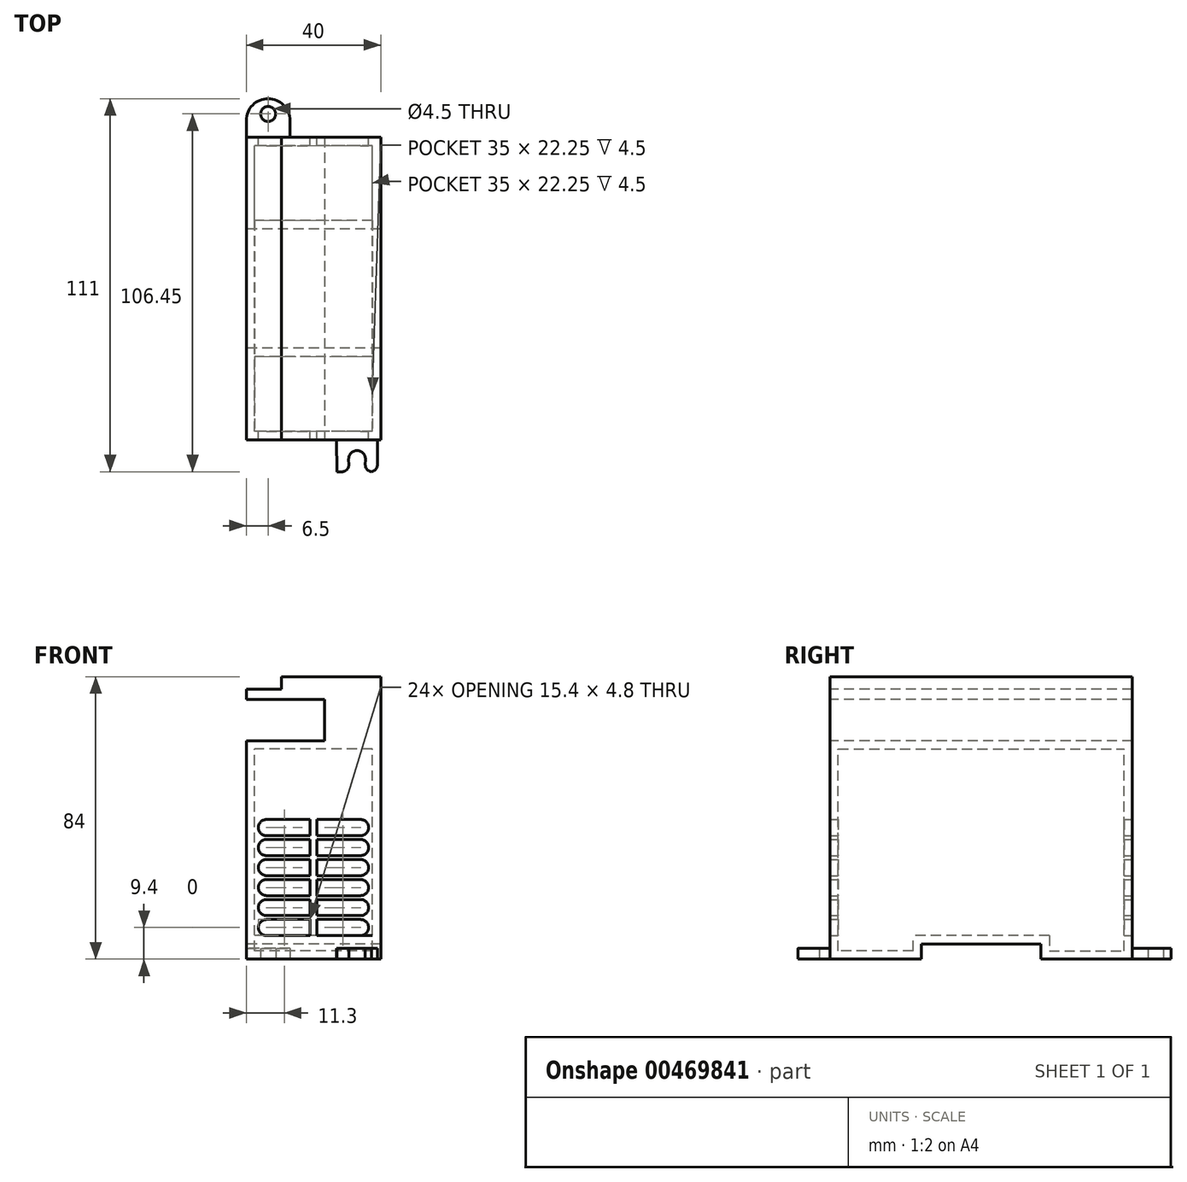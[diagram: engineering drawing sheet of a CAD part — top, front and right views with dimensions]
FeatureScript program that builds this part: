
annotation { "Feature Type Name" : "Feature", "Feature Type Description" : "" }
export const myFeature = defineFeature(function(context is Context, id is Id, definition is map)
    precondition{}
    {
        {
            var Q0;
            Q0=qCreatedBy(makeId("Right.planeOp"),FACE);
            var sketch = newSketch(context, id + "F0", { "sketchPlane" : qUnion([Q0])});
            skLineSegment(sketch, "E0", {"start": v(-17.75, 0) * mm, "end": v(-45, 0) * mm});
            skLineSegment(sketch, "E1", {"start": v(17.75, 0) * mm, "end": v(45, 0) * mm});
            skLineSegment(sketch, "E2", {"start": v(-45, 0) * mm, "end": v(-45, 65) * mm});
            skLineSegment(sketch, "E3", {"start": v(45, 0) * mm, "end": v(45, 65) * mm});
            skLineSegment(sketch, "E4", {"start": v(-45, 65) * mm, "end": v(45, 65) * mm});
            skLineSegment(sketch, "E5", {"start": v(-17.75, 0) * mm, "end": v(-17.75, 4.5) * mm});
            skLineSegment(sketch, "E6", {"start": v(17.75, 4.5) * mm, "end": v(17.75, 0) * mm});
            skLineSegment(sketch, "E7", {"start": v(17.75, 4.5) * mm, "end": v(-17.75, 4.5) * mm});
            skSolve(sketch);
        }
        {
            var Q0;
            Q0=makeQuery(id+"F0.imprint","IMPRINT",FACE,{"disambiguationData":[TD([[makeQuery(id+"F0.imprint","IMPRINT",EDGE,{"derivedFrom":sQuery(id+"F0.wireOp",EDGE,"E0")}),-1.0]])]});
            extrude(context, id + "F1", {"entities" : qUnion([Q0]), "depth" : 40 * mm});
        }
        {
            var Q0;
            Q0=makeQuery(id+"F1.opExtrude","SWEPT_FACE",FACE,{"disambiguationData":[OSD([sQuery(id+"F0.wireOp",EDGE,"E3")])]});
            var sketch = newSketch(context, id + "F2", { "sketchPlane" : qUnion([Q0])});
            skLineSegment(sketch, "E8", {"start": v(-20, 0) * mm, "end": v(-20, 7) * mm});
            skLineSegment(sketch, "E9", {"start": v(-19, 7) * mm, "end": v(-21, 7) * mm});
            skLineSegment(sketch, "E10", {"start": v(-21, 7) * mm, "end": v(-21, 11.8) * mm});
            skLineSegment(sketch, "E11", {"start": v(-21, 11.8) * mm, "end": v(-34, 11.8) * mm});
            skLineSegment(sketch, "E12", {"start": v(-21, 7) * mm, "end": v(-34, 7) * mm});
            skArc(sketch, "E13", {"start": v(-34, 7) * mm, "mid": v(-36.4, 9.4) * mm, "end": v(-34, 11.8) * mm});
            skPoint(sketch, "E13.centerSnap0", {"position": v(-21, 9.4) * mm});
            skLineSegment(sketch, "E14.MirrorCS", {"start": v(-19, 11.8) * mm, "end": v(-6, 11.8) * mm});
            skLineSegment(sketch, "E15.MirrorCS", {"start": v(-19, 7) * mm, "end": v(-19, 11.8) * mm});
            skLineSegment(sketch, "E16.MirrorCS", {"start": v(-19, 7) * mm, "end": v(-6, 7) * mm});
            skArc(sketch, "E17.MirrorCS", {"start": v(-6, 7) * mm, "mid": v(-3.6, 9.4) * mm, "end": v(-6, 11.8) * mm});
            skLineSegment(sketch, "E18.0.1.0", {"start": v(-21, 17.75) * mm, "end": v(-34, 17.75) * mm});
            skArc(sketch, "E18.0.1.1", {"start": v(-34, 12.95) * mm, "mid": v(-36.4, 15.35) * mm, "end": v(-34, 17.75) * mm});
            skLineSegment(sketch, "E18.0.1.2", {"start": v(-21, 12.95) * mm, "end": v(-34, 12.95) * mm});
            skLineSegment(sketch, "E18.0.1.3", {"start": v(-21, 12.95) * mm, "end": v(-21, 17.75) * mm});
            skLineSegment(sketch, "E18.0.1.4", {"start": v(-19, 12.95) * mm, "end": v(-19, 17.75) * mm});
            skLineSegment(sketch, "E18.0.1.5", {"start": v(-19, 12.95) * mm, "end": v(-6, 12.95) * mm});
            skArc(sketch, "E18.0.1.6", {"start": v(-6, 12.95) * mm, "mid": v(-3.6, 15.35) * mm, "end": v(-6, 17.75) * mm});
            skLineSegment(sketch, "E18.0.1.7", {"start": v(-19, 17.75) * mm, "end": v(-6, 17.75) * mm});
            skLineSegment(sketch, "E18.0.2.0", {"start": v(-21, 23.7) * mm, "end": v(-34, 23.7) * mm});
            skArc(sketch, "E18.0.2.1", {"start": v(-34, 18.9) * mm, "mid": v(-36.4, 21.3) * mm, "end": v(-34, 23.7) * mm});
            skLineSegment(sketch, "E18.0.2.2", {"start": v(-21, 18.9) * mm, "end": v(-34, 18.9) * mm});
            skLineSegment(sketch, "E18.0.2.3", {"start": v(-21, 18.9) * mm, "end": v(-21, 23.7) * mm});
            skLineSegment(sketch, "E18.0.2.4", {"start": v(-19, 18.9) * mm, "end": v(-19, 23.7) * mm});
            skLineSegment(sketch, "E18.0.2.5", {"start": v(-19, 18.9) * mm, "end": v(-6, 18.9) * mm});
            skArc(sketch, "E18.0.2.6", {"start": v(-6, 18.9) * mm, "mid": v(-3.6, 21.3) * mm, "end": v(-6, 23.7) * mm});
            skLineSegment(sketch, "E18.0.2.7", {"start": v(-19, 23.7) * mm, "end": v(-6, 23.7) * mm});
            skLineSegment(sketch, "E18.0.3.0", {"start": v(-21, 29.65) * mm, "end": v(-34, 29.65) * mm});
            skArc(sketch, "E18.0.3.1", {"start": v(-34, 24.85) * mm, "mid": v(-36.4, 27.25) * mm, "end": v(-34, 29.65) * mm});
            skLineSegment(sketch, "E18.0.3.2", {"start": v(-21, 24.85) * mm, "end": v(-34, 24.85) * mm});
            skLineSegment(sketch, "E18.0.3.3", {"start": v(-21, 24.85) * mm, "end": v(-21, 29.65) * mm});
            skLineSegment(sketch, "E18.0.3.4", {"start": v(-19, 24.85) * mm, "end": v(-19, 29.65) * mm});
            skLineSegment(sketch, "E18.0.3.5", {"start": v(-19, 24.85) * mm, "end": v(-6, 24.85) * mm});
            skArc(sketch, "E18.0.3.6", {"start": v(-6, 24.85) * mm, "mid": v(-3.6, 27.25) * mm, "end": v(-6, 29.65) * mm});
            skLineSegment(sketch, "E18.0.3.7", {"start": v(-19, 29.65) * mm, "end": v(-6, 29.65) * mm});
            skLineSegment(sketch, "E18.0.4.0", {"start": v(-21, 35.6) * mm, "end": v(-34, 35.6) * mm});
            skArc(sketch, "E18.0.4.1", {"start": v(-34, 30.8) * mm, "mid": v(-36.4, 33.2) * mm, "end": v(-34, 35.6) * mm});
            skLineSegment(sketch, "E18.0.4.2", {"start": v(-21, 30.8) * mm, "end": v(-34, 30.8) * mm});
            skLineSegment(sketch, "E18.0.4.3", {"start": v(-21, 30.8) * mm, "end": v(-21, 35.6) * mm});
            skLineSegment(sketch, "E18.0.4.4", {"start": v(-19, 30.8) * mm, "end": v(-19, 35.6) * mm});
            skLineSegment(sketch, "E18.0.4.5", {"start": v(-19, 30.8) * mm, "end": v(-6, 30.8) * mm});
            skArc(sketch, "E18.0.4.6", {"start": v(-6, 30.8) * mm, "mid": v(-3.6, 33.2) * mm, "end": v(-6, 35.6) * mm});
            skLineSegment(sketch, "E18.0.4.7", {"start": v(-19, 35.6) * mm, "end": v(-6, 35.6) * mm});
            skLineSegment(sketch, "E18.0.5.0", {"start": v(-21, 41.55) * mm, "end": v(-34, 41.55) * mm});
            skArc(sketch, "E18.0.5.1", {"start": v(-34, 36.75) * mm, "mid": v(-36.4, 39.15) * mm, "end": v(-34, 41.55) * mm});
            skLineSegment(sketch, "E18.0.5.2", {"start": v(-21, 36.75) * mm, "end": v(-34, 36.75) * mm});
            skLineSegment(sketch, "E18.0.5.3", {"start": v(-21, 36.75) * mm, "end": v(-21, 41.55) * mm});
            skLineSegment(sketch, "E18.0.5.4", {"start": v(-19, 36.75) * mm, "end": v(-19, 41.55) * mm});
            skLineSegment(sketch, "E18.0.5.5", {"start": v(-19, 36.75) * mm, "end": v(-6, 36.75) * mm});
            skArc(sketch, "E18.0.5.6", {"start": v(-6, 36.75) * mm, "mid": v(-3.6, 39.15) * mm, "end": v(-6, 41.55) * mm});
            skLineSegment(sketch, "E18.0.5.7", {"start": v(-19, 41.55) * mm, "end": v(-6, 41.55) * mm});
            skLineSegment(sketch, "E18.direction1", {"start": v(-34, 11.8) * mm, "end": v(-9, 11.8) * mm, "construction": true});
            skLineSegment(sketch, "E18.direction2", {"start": v(-34, 11.8) * mm, "end": v(-34, 17.75) * mm, "construction": true});
            skSolve(sketch);
        }
        {
            var Q0;
            Q0=makeQuery(id+"F4.boolean.opBoolean","COPY",FACE,{"derivedFrom":makeQuery(id+"F4.opExtrude","SWEPT_FACE",FACE,{"disambiguationData":[OSD([sQuery(id+"F2.wireOp",EDGE,"E18.0.5.6")])]})});
            var Q1;
            Q1=makeQuery(id+"F4.boolean.opBoolean","COPY",FACE,{"derivedFrom":makeQuery(id+"F4.opExtrude","SWEPT_FACE",FACE,{"disambiguationData":[OSD([sQuery(id+"F2.wireOp",EDGE,"E18.0.4.6")])]})});
            var Q2;
            Q2=makeQuery(id+"F4.boolean.opBoolean","COPY",FACE,{"derivedFrom":makeQuery(id+"F4.opExtrude","SWEPT_FACE",FACE,{"disambiguationData":[OSD([sQuery(id+"F2.wireOp",EDGE,"E18.0.3.6")])]})});
            var Q3;
            Q3=makeQuery(id+"F4.boolean.opBoolean","COPY",FACE,{"derivedFrom":makeQuery(id+"F4.opExtrude","SWEPT_FACE",FACE,{"disambiguationData":[OSD([sQuery(id+"F2.wireOp",EDGE,"E18.0.2.6")])]})});
            var Q4;
            Q4=makeQuery(id+"F4.boolean.opBoolean","COPY",FACE,{"derivedFrom":makeQuery(id+"F4.opExtrude","SWEPT_FACE",FACE,{"disambiguationData":[OSD([sQuery(id+"F2.wireOp",EDGE,"E18.0.1.6")])]})});
            var Q5;
            Q5=makeQuery(id+"F4.boolean.opBoolean","COPY",FACE,{"derivedFrom":makeQuery(id+"F4.opExtrude","SWEPT_FACE",FACE,{"disambiguationData":[OSD([sQuery(id+"F2.wireOp",EDGE,"E17.MirrorCS")])]})});
            var Q6;
            Q6=makeQuery(id+"F1.opExtrude","SWEPT_BODY",BODY,{"disambiguationData":[OSD([sQuery(id+"F0.wireOp",EDGE,"E0"),sQuery(id+"F0.wireOp",EDGE,"E1"),sQuery(id+"F0.wireOp",EDGE,"E2"),sQuery(id+"F0.wireOp",EDGE,"E3"),sQuery(id+"F0.wireOp",EDGE,"E4"),sQuery(id+"F0.wireOp",EDGE,"E5"),sQuery(id+"F0.wireOp",EDGE,"E6"),sQuery(id+"F0.wireOp",EDGE,"E7")])]});
            shell(context, id + "F3", {"isHollow" : true, "entities" : qUnion([Q0, Q1, Q2, Q3, Q4, Q5]), "parts" : qUnion([Q6]), "thickness" : 2.5 * mm});
        }
        {
            var Q0;
            Q0=makeQuery(id+"F2.imprint","IMPRINT",FACE,{"disambiguationData":[TD([[makeQuery(id+"F2.imprint","IMPRINT",EDGE,{"derivedFrom":sQuery(id+"F2.wireOp",EDGE,"E18.0.5.0")}),1.0]])]});
            var Q1;
            Q1=makeQuery(id+"F2.imprint","IMPRINT",FACE,{"disambiguationData":[TD([[makeQuery(id+"F2.imprint","IMPRINT",EDGE,{"derivedFrom":sQuery(id+"F2.wireOp",EDGE,"E18.0.5.4")}),-1.0]])]});
            var Q2;
            Q2=makeQuery(id+"F2.imprint","IMPRINT",FACE,{"disambiguationData":[TD([[makeQuery(id+"F2.imprint","IMPRINT",EDGE,{"derivedFrom":sQuery(id+"F2.wireOp",EDGE,"E18.0.4.4")}),-1.0]])]});
            var Q3;
            Q3=makeQuery(id+"F2.imprint","IMPRINT",FACE,{"disambiguationData":[TD([[makeQuery(id+"F2.imprint","IMPRINT",EDGE,{"derivedFrom":sQuery(id+"F2.wireOp",EDGE,"E18.0.4.0")}),1.0]])]});
            var Q4;
            Q4=makeQuery(id+"F2.imprint","IMPRINT",FACE,{"disambiguationData":[TD([[makeQuery(id+"F2.imprint","IMPRINT",EDGE,{"derivedFrom":sQuery(id+"F2.wireOp",EDGE,"E18.0.3.0")}),1.0]])]});
            var Q5;
            Q5=makeQuery(id+"F2.imprint","IMPRINT",FACE,{"disambiguationData":[TD([[makeQuery(id+"F2.imprint","IMPRINT",EDGE,{"derivedFrom":sQuery(id+"F2.wireOp",EDGE,"E18.0.3.4")}),-1.0]])]});
            var Q6;
            Q6=makeQuery(id+"F2.imprint","IMPRINT",FACE,{"disambiguationData":[TD([[makeQuery(id+"F2.imprint","IMPRINT",EDGE,{"derivedFrom":sQuery(id+"F2.wireOp",EDGE,"E18.0.2.0")}),1.0]])]});
            var Q7;
            Q7=makeQuery(id+"F2.imprint","IMPRINT",FACE,{"disambiguationData":[TD([[makeQuery(id+"F2.imprint","IMPRINT",EDGE,{"derivedFrom":sQuery(id+"F2.wireOp",EDGE,"E18.0.2.4")}),-1.0]])]});
            var Q8;
            Q8=makeQuery(id+"F2.imprint","IMPRINT",FACE,{"disambiguationData":[TD([[makeQuery(id+"F2.imprint","IMPRINT",EDGE,{"derivedFrom":sQuery(id+"F2.wireOp",EDGE,"E18.0.1.0")}),1.0]])]});
            var Q9;
            Q9=makeQuery(id+"F2.imprint","IMPRINT",FACE,{"disambiguationData":[TD([[makeQuery(id+"F2.imprint","IMPRINT",EDGE,{"derivedFrom":sQuery(id+"F2.wireOp",EDGE,"E18.0.1.4")}),-1.0]])]});
            var Q10;
            Q10=makeQuery(id+"F2.imprint","IMPRINT",FACE,{"disambiguationData":[TD([[makeQuery(id+"F2.imprint","IMPRINT",EDGE,{"derivedFrom":sQuery(id+"F2.wireOp",EDGE,"E10")}),1.0]])]});
            var Q11;
            Q11=makeQuery(id+"F2.imprint","IMPRINT",FACE,{"disambiguationData":[TD([[makeQuery(id+"F2.imprint","IMPRINT",EDGE,{"derivedFrom":sQuery(id+"F2.wireOp",EDGE,"E14.MirrorCS")}),-1.0]])]});
            extrude(context, id + "F4", {"entities" : qUnion([Q0, Q1, Q2, Q3, Q4, Q5, Q6, Q7, Q8, Q9, Q10, Q11]), "operationType" : NewBodyOperationType.REMOVE, "endBound" : BoundingType.THROUGH_ALL, "oppositeDirection" : true, "depth" : 25 * mm});
        }
        {
            var Q0;
            Q0=makeQuery(id+"F1.opExtrude","SWEPT_FACE",FACE,{"disambiguationData":[OSD([sQuery(id+"F0.wireOp",EDGE,"E2")])]});
            var sketch = newSketch(context, id + "F5", { "sketchPlane" : qUnion([Q0])});
            skLineSegment(sketch, "E19", {"start": v(40, 65) * mm, "end": v(40, 84) * mm});
            skLineSegment(sketch, "E20", {"start": v(40, 84) * mm, "end": v(10.5, 84) * mm});
            skLineSegment(sketch, "E21", {"start": v(10.5, 84) * mm, "end": v(10.5, 80.25) * mm});
            skLineSegment(sketch, "E22", {"start": v(10.5, 80.25) * mm, "end": v(0, 80.25) * mm});
            skLineSegment(sketch, "E23", {"start": v(0, 80.25) * mm, "end": v(0, 77.25) * mm});
            skLineSegment(sketch, "E24", {"start": v(0, 77.25) * mm, "end": v(23.3, 77.25) * mm});
            skLineSegment(sketch, "E25", {"start": v(23.3, 77.25) * mm, "end": v(23.3, 65) * mm});
            skSolve(sketch);
        }
        {
            var Q0;
            {var subQ0=sQuery(id+"F5.wireOp",EDGE,"E19");Q0=makeQuery(id+"F5.imprint","IMPRINT",FACE,{"disambiguationData":[TD([[makeQuery(id+"F5.imprint","IMPRINT",EDGE,{"derivedFrom":subQ0}),1.0]])]});}
            extrude(context, id + "F6", {"entities" : qUnion([Q0]), "operationType" : NewBodyOperationType.ADD, "oppositeDirection" : true, "depth" : 90 * mm});
        }
        {
            var Q0;
            Q0=qCreatedBy(makeId("Top.planeOp"),FACE);
            var sketch = newSketch(context, id + "F7", { "sketchPlane" : qUnion([Q0])});
            skLineSegment(sketch, "E26", {"start": v(0, 45) * mm, "end": v(0, 50) * mm});
            skLineSegment(sketch, "E27", {"start": v(0, 45) * mm, "end": v(13, 45) * mm});
            skLineSegment(sketch, "E28", {"start": v(13, 45) * mm, "end": v(13, 50) * mm});
            skArc(sketch, "E29", {"start": v(13, 50) * mm, "mid": v(6.5, 56.5) * mm, "end": v(0, 50) * mm});
            skCircle(sketch, "E30", {"center": v(6.5, 51.95) * mm, "radius": 2.25 * mm});
            skLineSegment(sketch, "E31", {"start": v(39.98, -45) * mm, "end": v(38.98, -45) * mm});
            skLineSegment(sketch, "E32", {"start": v(38.98, -45) * mm, "end": v(26.78, -45) * mm});
            skLineSegment(sketch, "E33", {"start": v(26.78, -45) * mm, "end": v(26.92, -54.5) * mm});
            skLineSegment(sketch, "E34", {"start": v(26.92, -54.5) * mm, "end": v(38.98, -54.5) * mm});
            skLineSegment(sketch, "E35", {"start": v(38.98, -54.5) * mm, "end": v(38.98, -45) * mm});
            skCircle(sketch, "E36", {"center": v(32.95, -50.7) * mm, "radius": 2.5 * mm});
            skPoint(sketch, "E36.centerSnap0", {"position": v(32.95, -54.5) * mm});
            skLineSegment(sketch, "E37", {"start": v(30.45, -50.76) * mm, "end": v(30.53, -54.5) * mm});
            skLineSegment(sketch, "E38", {"start": v(35.45, -50.76) * mm, "end": v(35.36, -54.5) * mm});
            skSolve(sketch);
        }
        {
            var Q0;
            Q0=makeQuery(id+"F7.imprint","IMPRINT",FACE,{"disambiguationData":[TD([[makeQuery(id+"F7.imprint","IMPRINT",EDGE,{"derivedFrom":sQuery(id+"F7.wireOp",EDGE,"E26")}),-1.0]])]});
            var Q1;
            Q1=makeQuery(id+"F7.imprint","IMPRINT",FACE,{"disambiguationData":[TD([[makeQuery(id+"F7.imprint","IMPRINT",EDGE,{"derivedFrom":sQuery(id+"F7.wireOp",EDGE,"E32")}),1.0]])]});
            extrude(context, id + "F8", {"entities" : qUnion([Q0, Q1]), "depth" : 3.2 * mm});
        }
        {
            var Q0;
            Q0=makeQuery(id+"F8.opExtrude","SWEPT_EDGE",EDGE,{"disambiguationData":[OSD([sQuery(id+"F7.wireOp",EDGE,"E34"),sQuery(id+"F7.wireOp",EDGE,"E37")])]});
            var Q1;
            Q1=makeQuery(id+"F8.opExtrude","SWEPT_EDGE",EDGE,{"disambiguationData":[OSD([sQuery(id+"F7.wireOp",EDGE,"E34"),sQuery(id+"F7.wireOp",EDGE,"E38")])]});
            var Q2;
            Q2=makeQuery(id+"F8.opExtrude","SWEPT_EDGE",EDGE,{"disambiguationData":[OSD([sQuery(id+"F7.wireOp",EDGE,"E34"),sQuery(id+"F7.wireOp",EDGE,"E35")])]});
            fillet(context, id + "F9", {"entities" : qUnion([Q0, Q1, Q2]), "radius" : 2 * mm, "tangentPropagation" : true, "allowEdgeOverflow" : false});
        }
    });
